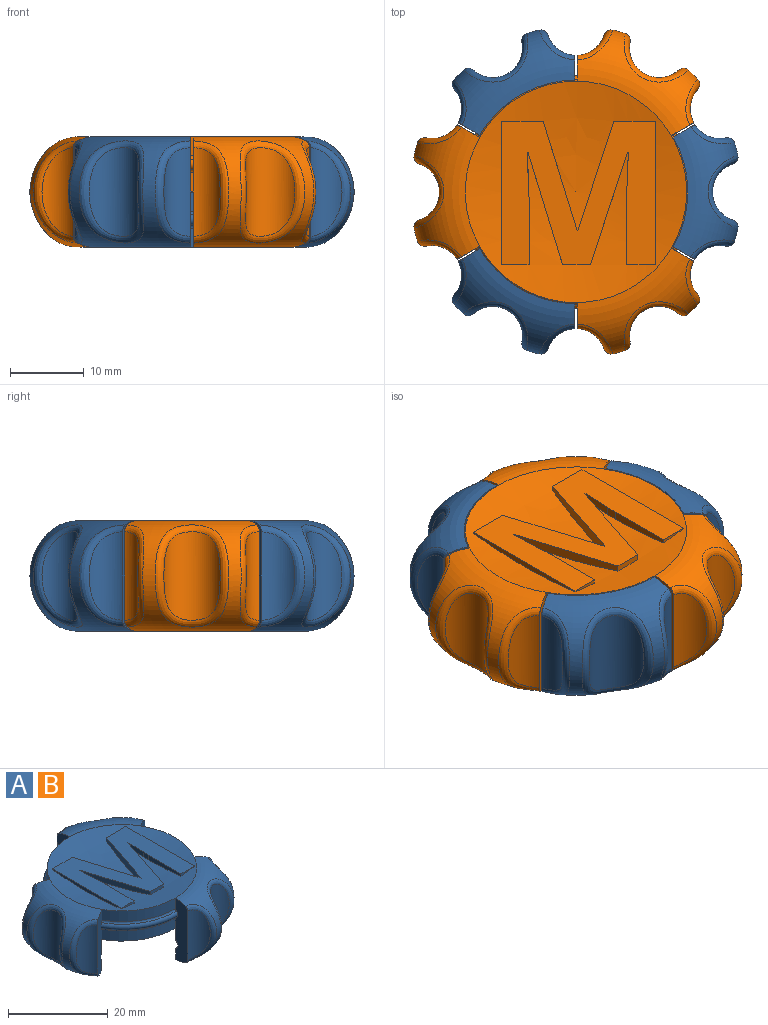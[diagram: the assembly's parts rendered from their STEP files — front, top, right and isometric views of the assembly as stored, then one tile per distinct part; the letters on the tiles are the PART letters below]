
ASSEMBLY  parts=2 mates=1
PART A: 81 faces, bbox 63.8x69x31 mm
  f0: cylinder r=15.15mm len=14.89mm, axis (0,0,1), area 38.4mm2, adj f1,f76,f77,f78
  f1: plane 31.01x19.04mm, normal (0.5,-0.87,0), area 47.5mm2, adj f0,f2,f62,f63,f64,f65,f66,f67
  f2: cylinder r=15mm len=13.21mm, axis (0,0,-1), area 41.7mm2, adj f1,f3,f61,f62
  f3: sphere r=75.75mm, area 451.4mm2, adj f2,f4,f6,f7,f8,f9,f10,f11
  f4: plane 15.25x4.68mm, normal (-0.96,-0.29,0), area 19.3mm2, adj f3,f5,f6,f23
  f5: plane 20.79x19.45mm, normal (0,0,1), area 260.8mm2, adj f4,f6,f7,f8,f9,f10,f11,f12
  f6: plane 1.03x0.12mm, normal (0,-1,0), area 0.1mm2, adj f3,f4,f5,f7
  f7: extruded ~6.21x1.23mm, area 7.3mm2, adj f3,f5,f6,f8
  f8: plane 9.04x1.23mm, normal (1,0,0), area 9mm2, adj f3,f5,f7,f9
  f9: plane 3.69x0.59mm, normal (0,-1,0), area 1.5mm2, adj f3,f5,f8,f10
  f10: plane 19.45x0.83mm, normal (-1,0,0), area 12mm2, adj f3,f5,f9,f11
  f11: plane 5.61x0.76mm, normal (0,1,0), area 2.9mm2, adj f3,f5,f10,f12
  f12: plane 14.87x4.6mm, normal (0.96,0.3,0), area 20.3mm2, adj f3,f5,f11,f13
  f13: plane 1.32x0.08mm, normal (0,1,0), area 0.1mm2, adj f3,f5,f12,f14
  f14: plane 14.87x4.88mm, normal (-0.95,0.31,0), area 20.1mm2, adj f3,f5,f13,f15
  f15: plane 5.61x0.72mm, normal (0,1,0), area 2.5mm2, adj f3,f5,f14,f16
  f16: plane 19.45x0.74mm, normal (1,0,0), area 10.2mm2, adj f3,f5,f15,f17
  f17: plane 3.84x0.54mm, normal (0,-1,0), area 1.3mm2, adj f3,f5,f16,f18
  f18: plane 9.21x1.18mm, normal (-1,0,0), area 8.8mm2, adj f3,f5,f17,f19
  f19: extruded ~1.5x1.18mm, area 1.8mm2, adj f3,f5,f18,f20
  f20: extruded ~4.52x1.18mm, area 5mm2, adj f3,f5,f19,f21
  f21: plane 0.99x0.12mm, normal (0,-1,0), area 0.1mm2, adj f3,f5,f20,f22
  f22: plane 15.23x5.01mm, normal (0.95,-0.31,0), area 19.1mm2, adj f3,f5,f21,f23
  f23: plane 3.78x0.86mm, normal (0,-1,0), area 3.2mm2, adj f3,f4,f5,f22
  f24: cylinder r=15mm len=13.21mm, axis (0,0,-1), area 41.7mm2, adj f3,f25,f29,f77
  f25: torus R=15.5mm, axis (0,0,-1), area 9.3mm2, adj f24,f26,f29,f77
  f26: torus R=15mm, axis (0,0,-1), area 28.9mm2, adj f25,f27,f29,f77
  f27: torus R=15.5mm, axis (0,0,-1), area 9.3mm2, adj f26,f28,f29,f77
  f28: cylinder r=15mm len=13.21mm, axis (0,0,-1), area 40.1mm2, adj f27,f29,f77,f78
  f29: plane 31.01x19.51mm, normal (-1,0,0), area 47.5mm2, adj f24,f25,f26,f27,f28,f30,f46,f47
  f30: cylinder r=15.15mm len=12.89mm, axis (0,0,1), area 38.4mm2, adj f29,f31,f46,f78
  f31: plane 31x19.04mm, normal (0.5,-0.87,0), area 47.5mm2, adj f30,f32,f41,f42,f43,f44,f45,f46
  f32: cylinder r=15mm len=15.26mm, axis (0,0,-1), area 40.1mm2, adj f31,f33,f41,f78
  f33: plane 31.01x19.04mm, normal (0.5,0.87,0), area 47.5mm2, adj f32,f34,f35,f36,f37,f38,f39,f40
  f34: cylinder r=15.15mm len=12.89mm, axis (0,0,1), area 38.4mm2, adj f33,f35,f61,f78
  f35: torus R=16.15mm, axis (0,0,1), area 13.8mm2, adj f33,f34,f36,f61
  f36: torus R=15mm, axis (0,0,1), area 22.7mm2, adj f33,f35,f37,f61
  f37: torus R=16.15mm, axis (0,0,1), area 13.8mm2, adj f33,f36,f38,f61
  f38: cylinder r=15.15mm len=12.89mm, axis (0,0,1), area 36.8mm2, adj f33,f37,f52,f61
  f39: bspline ~13.85x6.8mm, area 25mm2, adj f33,f40,f52
  f40: cylinder r=4mm len=11.99mm, axis (0,0,1), area 0mm2, adj f33,f39
  f41: torus R=15.5mm, axis (0,0,-1), area 9.3mm2, adj f31,f32,f33,f42
  f42: torus R=15mm, axis (0,0,-1), area 28.9mm2, adj f31,f33,f41,f43
  f43: torus R=15.5mm, axis (0,0,-1), area 9.3mm2, adj f31,f33,f42,f57
  f44: bspline ~13.85x6.8mm, area 25mm2, adj f31,f45,f58
  f45: cylinder r=4mm len=11.99mm, axis (0,0,1), area 0mm2, adj f31,f44
  f46: torus R=16.15mm, axis (0,0,1), area 13.8mm2, adj f29,f30,f31,f47
  f47: torus R=15mm, axis (0,0,1), area 22.7mm2, adj f29,f31,f46,f48
  f48: torus R=16.15mm, axis (0,0,1), area 13.8mm2, adj f29,f31,f47,f49
  f49: cylinder r=15.15mm len=12.89mm, axis (0,0,1), area 36.8mm2, adj f29,f31,f48,f58
  f50: bspline ~13.85x5.54mm, area 25mm2, adj f29,f51,f58
  f51: cylinder r=4mm len=11.99mm, axis (0,0,1), area 0mm2, adj f29,f50
  f52: torus R=15mm, axis (0,0,-1), area 197.5mm2, adj f3,f33,f38,f39,f53,f55,f61
  f53: bspline ~13.85x5.54mm, area 25mm2, adj f52,f54,f61
  f54: cylinder r=4mm len=11.99mm, axis (0,0,1), area 0mm2, adj f53,f61
  f55: bspline ~13.85x8.79mm, area 50.7mm2, adj f52,f56
  f56: cylinder r=4mm len=12mm, axis (0,0,1), area 97.2mm2, adj f55
  f57: cylinder r=15mm len=15.26mm, axis (0,0,-1), area 41.7mm2, adj f3,f31,f33,f43
  f58: torus R=15mm, axis (0,0,-1), area 197.6mm2, adj f3,f29,f31,f44,f49,f50,f59
  f59: bspline ~13.85x8.79mm, area 50.7mm2, adj f58,f60
  f60: cylinder r=4mm len=12mm, axis (0,0,1), area 97.2mm2, adj f59
  f61: plane 31x19.51mm, normal (-1,0,0), area 47.5mm2, adj f2,f34,f35,f36,f37,f38,f52,f53
  f62: torus R=15.5mm, axis (0,0,-1), area 9.3mm2, adj f1,f2,f61,f63
  f63: torus R=15mm, axis (0,0,-1), area 28.9mm2, adj f1,f61,f62,f64
  f64: torus R=15.5mm, axis (0,0,-1), area 9.3mm2, adj f1,f61,f63,f65
  f65: cylinder r=15mm len=13.21mm, axis (0,0,-1), area 40.1mm2, adj f1,f61,f64,f78
  f66: torus R=15mm, axis (0,0,1), area 22.7mm2, adj f1,f67,f76,f77
  f67: torus R=16.15mm, axis (0,0,1), area 13.8mm2, adj f1,f66,f68,f77
  f68: cylinder r=15.15mm len=14.89mm, axis (0,0,1), area 36.8mm2, adj f1,f67,f69,f77
  f69: torus R=15mm, axis (0,0,-1), area 197.5mm2, adj f1,f3,f68,f70,f72,f74,f77
  f70: bspline ~13.85x6.3mm, area 25mm2, adj f69,f71,f77
  f71: cylinder r=4mm len=11.99mm, axis (0,0,1), area 0mm2, adj f70,f77
  f72: bspline ~13.85x9.96mm, area 50.7mm2, adj f69,f73
  f73: cylinder r=4mm len=12mm, axis (0,0,1), area 97.2mm2, adj f72
  f74: bspline ~13.85x6.3mm, area 25mm2, adj f1,f69,f75
  f75: cylinder r=4mm len=11.99mm, axis (0,0,1), area 0mm2, adj f1,f74
  f76: torus R=16.15mm, axis (0,0,1), area 13.8mm2, adj f0,f1,f66,f77
  f77: plane 31x19.04mm, normal (0.5,0.87,0), area 47.5mm2, adj f0,f24,f25,f26,f27,f28,f66,f67
  f78: plane 30.3x30.15mm, normal (0,0,-1), area 98.1mm2, adj f0,f1,f28,f29,f30,f31,f32,f33
  f79: cone r=12mm half-angle=45deg, axis (0,0,-1), area 220.3mm2, adj f78,f80
  f80: plane 24.2x24.2mm, normal (0,0,-1), area 460mm2, adj f79
PART B: same geometry as A
PLACE A rot(axis=(0,1,0),180deg) t=(40.64,-1.46,-4.1)mm
PLACE B t=(40.64,-1.46,-4.1)mm
MATE fastened A.f26 <-> B.f26  axis (0,0,1) through (40.64,-1.46,-4.2)mm
